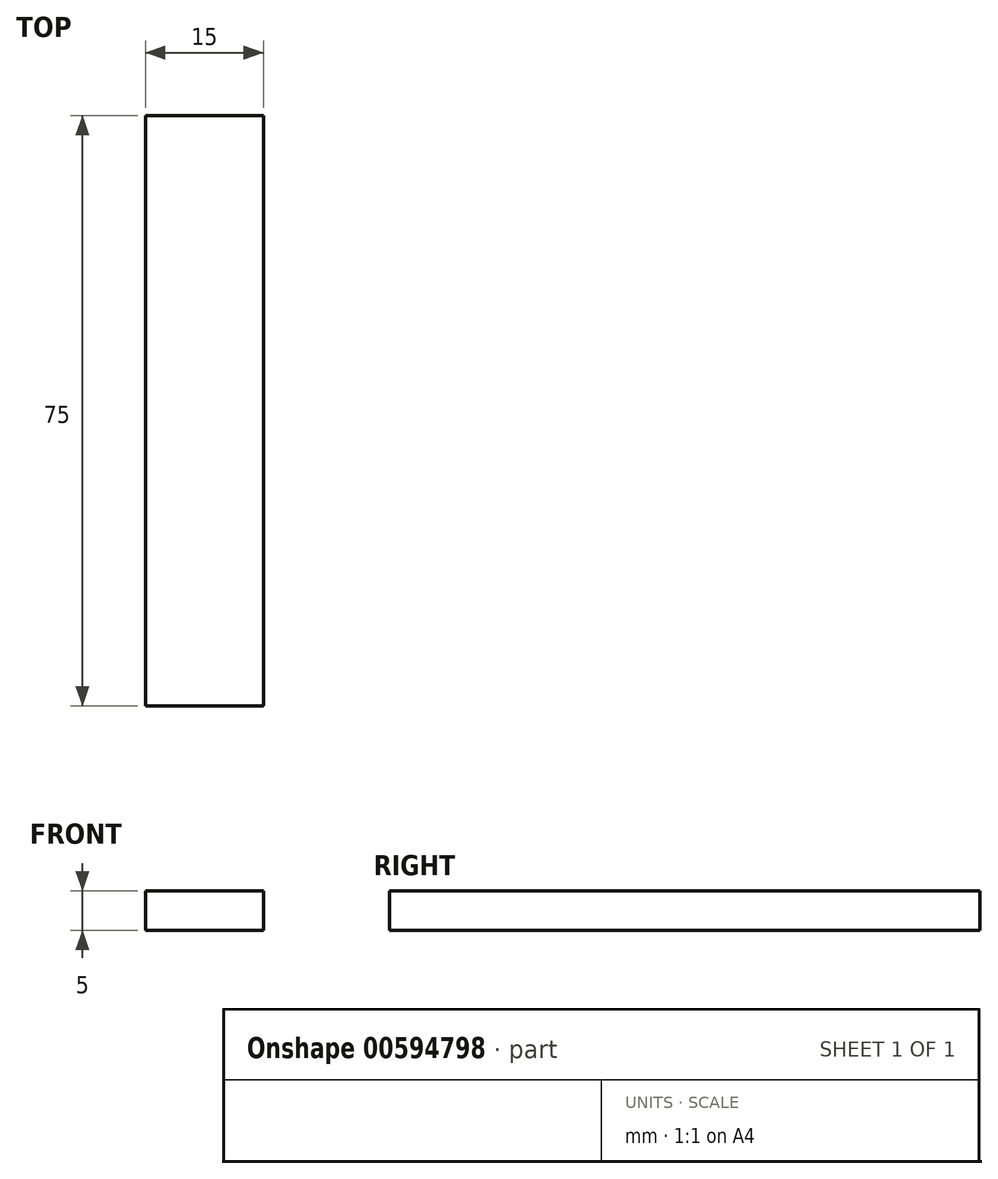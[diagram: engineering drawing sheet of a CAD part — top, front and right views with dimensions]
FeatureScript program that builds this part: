
annotation { "Feature Type Name" : "Feature", "Feature Type Description" : "" }
export const myFeature = defineFeature(function(context is Context, id is Id, definition is map)
    precondition{}
    {
        {
            var Q0;
            Q0=qCreatedBy(makeId("Top.planeOp"),FACE);
            var sketch = newSketch(context, id + "F0", { "sketchPlane" : qUnion([Q0])});
            skLineSegment(sketch, "E0.bottom", {"start": v(-8.94, 55.23) * mm, "end": v(6.06, 55.23) * mm});
            skLineSegment(sketch, "E0.top", {"start": v(-8.94, -19.77) * mm, "end": v(6.06, -19.77) * mm});
            skLineSegment(sketch, "E0.left", {"start": v(-8.94, 55.23) * mm, "end": v(-8.94, -19.77) * mm});
            skLineSegment(sketch, "E0.right", {"start": v(6.06, 55.23) * mm, "end": v(6.06, -19.77) * mm});
            skSolve(sketch);
        }
        {
            var Q0;
            Q0=makeQuery(id+"F0.imprint","IMPRINT",FACE,{"disambiguationData":[TD([[makeQuery(id+"F0.imprint","IMPRINT",EDGE,{"derivedFrom":sQuery(id+"F0.wireOp",EDGE,"E0.bottom")}),-1.0]])]});
            extrude(context, id + "F1", {"entities" : qUnion([Q0]), "depth" : 5 * mm, "offsetDistance" : 25 * mm});
        }
    });
